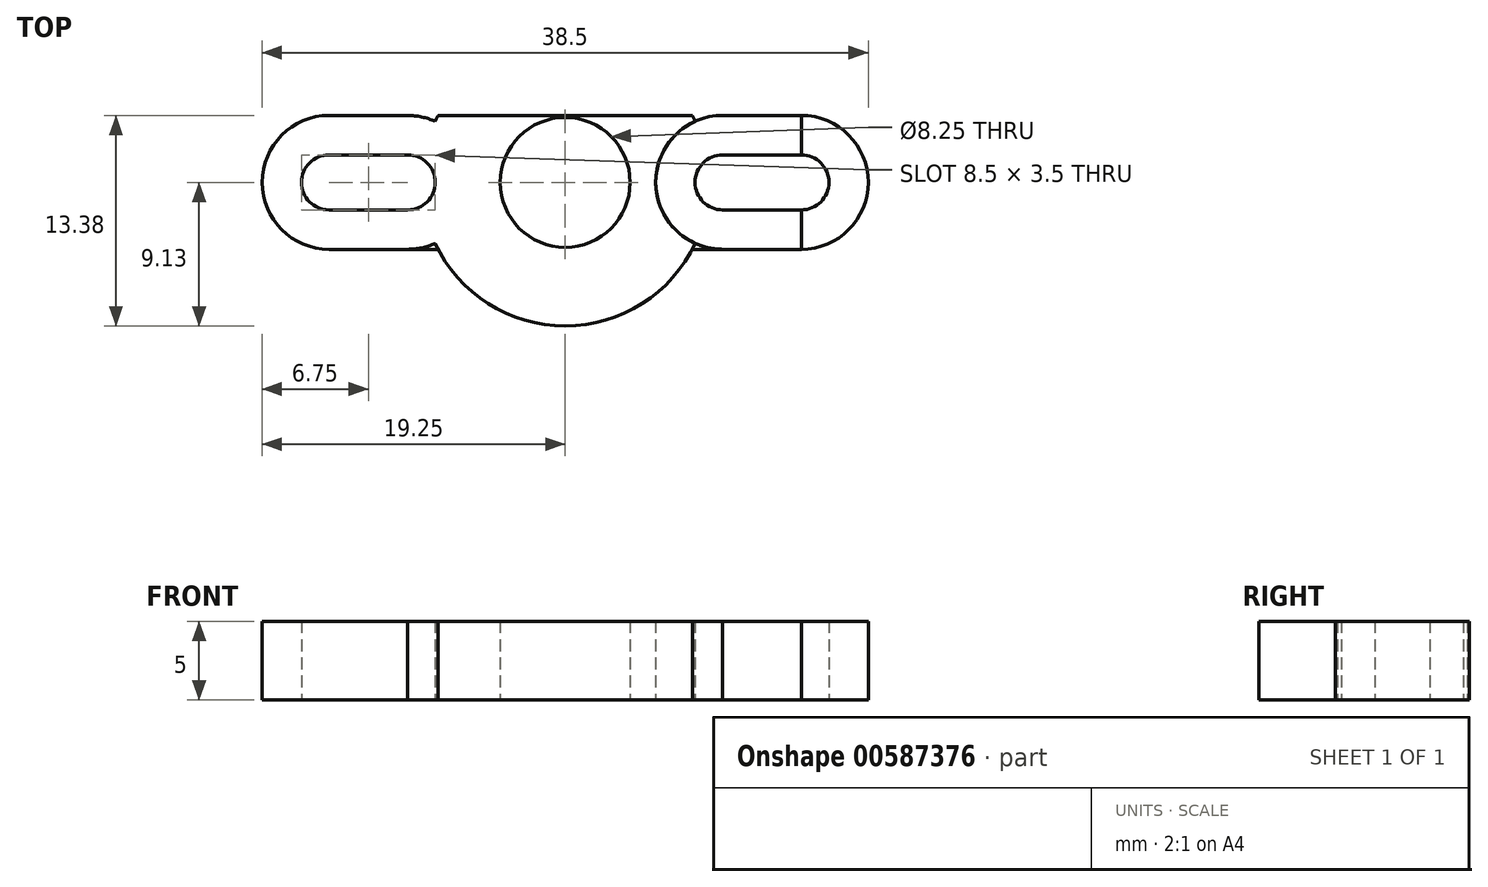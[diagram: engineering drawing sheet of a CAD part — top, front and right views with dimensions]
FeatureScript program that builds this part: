
annotation { "Feature Type Name" : "Feature", "Feature Type Description" : "" }
export const myFeature = defineFeature(function(context is Context, id is Id, definition is map)
    precondition{}
    {
        {
            var Q0;
            Q0=qCreatedBy(makeId("Top.planeOp"),FACE);
            var sketch = newSketch(context, id + "F0", { "sketchPlane" : qUnion([Q0])});
            skCircle(sketch, "E0", {"center": v(0, 0) * mm, "radius": 4.12 * mm});
            skCircle(sketch, "E1", {"center": v(10, 0) * mm, "radius": 1.75 * mm});
            skCircle(sketch, "E2", {"center": v(-10, 0) * mm, "radius": 1.75 * mm});
            skCircle(sketch, "E3", {"center": v(0, 0) * mm, "radius": 9.12 * mm});
            skCircle(sketch, "E4", {"center": v(15, 0) * mm, "radius": 1.75 * mm});
            skCircle(sketch, "E5", {"center": v(-15, 0) * mm, "radius": 1.75 * mm});
            skLineSegment(sketch, "E6.bottom", {"start": v(-15, 1.75) * mm, "end": v(-10, 1.75) * mm});
            skLineSegment(sketch, "E6.top", {"start": v(-15, -1.75) * mm, "end": v(-10, -1.75) * mm});
            skLineSegment(sketch, "E6.left", {"start": v(-15, 1.75) * mm, "end": v(-15, -1.75) * mm});
            skLineSegment(sketch, "E6.right", {"start": v(-10, 1.75) * mm, "end": v(-10, -1.75) * mm});
            skPoint(sketch, "E6.middle", {"position": v(-12.5, 0) * mm});
            skLineSegment(sketch, "E7.bottom", {"start": v(10, 1.75) * mm, "end": v(15, 1.75) * mm});
            skLineSegment(sketch, "E7.top", {"start": v(10, -1.75) * mm, "end": v(15, -1.75) * mm});
            skLineSegment(sketch, "E7.left", {"start": v(10, 1.75) * mm, "end": v(10, -1.75) * mm});
            skLineSegment(sketch, "E7.right", {"start": v(15, 1.75) * mm, "end": v(15, -1.75) * mm});
            skPoint(sketch, "E7.middle", {"position": v(12.5, 0) * mm});
            skCircle(sketch, "E8", {"center": v(-15, 0) * mm, "radius": 4.25 * mm});
            skCircle(sketch, "E9", {"center": v(15, 0) * mm, "radius": 4.25 * mm});
            skCircle(sketch, "E10", {"center": v(-10, 0) * mm, "radius": 4.25 * mm});
            skCircle(sketch, "E11", {"center": v(10, 0) * mm, "radius": 4.25 * mm});
            skLineSegment(sketch, "E12.bottom", {"start": v(-15, 4.25) * mm, "end": v(15, 4.25) * mm});
            skLineSegment(sketch, "E12.top", {"start": v(-15, -4.25) * mm, "end": v(15, -4.25) * mm});
            skLineSegment(sketch, "E12.left", {"start": v(-15, 4.25) * mm, "end": v(-15, -4.25) * mm});
            skLineSegment(sketch, "E12.right", {"start": v(15, 4.25) * mm, "end": v(15, -4.25) * mm});
            skSolve(sketch);
        }
        {
            var Q0;
            {var subQ0=sQuery(id+"F0.wireOp",EDGE,"E12.bottom");var subQ1=sQuery(id+"F0.wireOp",EDGE,"E3");var subQ2=makeQuery(id+"F0.imprint","INTERSECT",VERTEX,{"disambiguationData":[OD(0.0)],"derivedFrom":[subQ1,subQ0]});Q0=makeQuery(id+"F0.imprint","IMPRINT",FACE,{"disambiguationData":[TD([[makeQuery(id+"F0.imprint","IMPRINT",EDGE,{"disambiguationData":[TD([[subQ2,-1.0]])],"derivedFrom":subQ1}),1.0]])]});}
            var Q1;
            Q1=makeQuery(id+"F0.imprint","IMPRINT",FACE,{"disambiguationData":[TD([[makeQuery(id+"F0.imprint","IMPRINT",EDGE,{"derivedFrom":sQuery(id+"F0.wireOp",EDGE,"E0")}),-1.0]])]});
            var Q2;
            {var subQ0=sQuery(id+"F0.wireOp",EDGE,"E12.top");var subQ1=sQuery(id+"F0.wireOp",EDGE,"E3");var subQ2=makeQuery(id+"F0.imprint","INTERSECT",VERTEX,{"disambiguationData":[OD(0.0)],"derivedFrom":[subQ1,subQ0]});Q2=makeQuery(id+"F0.imprint","IMPRINT",FACE,{"disambiguationData":[TD([[makeQuery(id+"F0.imprint","IMPRINT",EDGE,{"disambiguationData":[TD([[subQ2,-1.0]])],"derivedFrom":subQ1}),1.0]])]});}
            var Q3;
            {var subQ0=sQuery(id+"F0.wireOp",EDGE,"E3");var subQ1=sQuery(id+"F0.wireOp",EDGE,"E2");var subQ2=makeQuery(id+"F0.imprint","INTERSECT",VERTEX,{"disambiguationData":[OD(0.0)],"derivedFrom":[subQ1,subQ0]});Q3=makeQuery(id+"F0.imprint","IMPRINT",FACE,{"disambiguationData":[TD([[makeQuery(id+"F0.imprint","IMPRINT",EDGE,{"disambiguationData":[TD([[subQ2,1.0]])],"derivedFrom":subQ1}),-1.0]])]});}
            var Q4;
            {var subQ5=sQuery(id+"F0.wireOp",EDGE,"E2");var subQ7=sQuery(id+"F0.wireOp",EDGE,"E3");var subQ8=makeQuery(id+"F0.imprint","INTERSECT",VERTEX,{"disambiguationData":[OD(0.0)],"derivedFrom":[subQ5,subQ7]});Q4=makeQuery(id+"F0.imprint","IMPRINT",FACE,{"disambiguationData":[TD([[makeQuery(id+"F0.imprint","IMPRINT",EDGE,{"disambiguationData":[TD([[subQ8,1.0]])],"derivedFrom":subQ7}),-1.0]])]});}
            var Q5;
            {var subQ0=sQuery(id+"F0.wireOp",EDGE,"E12.bottom");var subQ3=sQuery(id+"F0.wireOp",EDGE,"E10");var subQ5=makeQuery(id+"F0.imprint","INTERSECT",VERTEX,{"derivedFrom":[subQ3,subQ0]});Q5=makeQuery(id+"F0.imprint","IMPRINT",FACE,{"disambiguationData":[TD([[makeQuery(id+"F0.imprint","IMPRINT",EDGE,{"disambiguationData":[TD([[subQ5,-1.0]])],"derivedFrom":subQ3}),-1.0]])]});}
            var Q6;
            {var subQ1=sQuery(id+"F0.wireOp",EDGE,"E6.bottom");var subQ3=sQuery(id+"F0.wireOp",EDGE,"E10");var subQ4=makeQuery(id+"F0.imprint","INTERSECT",VERTEX,{"derivedFrom":[subQ1,subQ3]});Q6=makeQuery(id+"F0.imprint","IMPRINT",FACE,{"disambiguationData":[TD([[makeQuery(id+"F0.imprint","IMPRINT",EDGE,{"disambiguationData":[TD([[subQ4,1.0]])],"derivedFrom":subQ3}),-1.0]])]});}
            var Q7;
            {var subQ0=sQuery(id+"F0.wireOp",EDGE,"E12.left");var subQ1=sQuery(id+"F0.wireOp",EDGE,"E5");var subQ2=makeQuery(id+"F0.imprint","INTERSECT",VERTEX,{"derivedFrom":[subQ1,sQuery(id+"F0.wireOp",EDGE,"E6.bottom"),subQ0]});Q7=makeQuery(id+"F0.imprint","IMPRINT",FACE,{"disambiguationData":[TD([[makeQuery(id+"F0.imprint","IMPRINT",EDGE,{"disambiguationData":[TD([[subQ2,-1.0]])],"derivedFrom":subQ1}),-1.0]])]});}
            var Q8;
            {var subQ0=sQuery(id+"F0.wireOp",EDGE,"E10");var subQ1=sQuery(id+"F0.wireOp",EDGE,"E6.bottom");var subQ2=makeQuery(id+"F0.imprint","INTERSECT",VERTEX,{"derivedFrom":[subQ1,subQ0]});Q8=makeQuery(id+"F0.imprint","IMPRINT",FACE,{"disambiguationData":[TD([[makeQuery(id+"F0.imprint","IMPRINT",EDGE,{"disambiguationData":[TD([[subQ2,-1.0]])],"derivedFrom":subQ1}),1.0]])]});}
            var Q9;
            {var subQ3=sQuery(id+"F0.wireOp",EDGE,"E8");var subQ11=sQuery(id+"F0.wireOp",EDGE,"E2");var subQ12=makeQuery(id+"F0.imprint","INTERSECT",VERTEX,{"disambiguationData":[OD(0.0)],"derivedFrom":[subQ11,subQ3]});Q9=makeQuery(id+"F0.imprint","IMPRINT",FACE,{"disambiguationData":[TD([[makeQuery(id+"F0.imprint","IMPRINT",EDGE,{"disambiguationData":[TD([[subQ12,-1.0]])],"derivedFrom":subQ11}),-1.0]])]});}
            var Q10;
            {var subQ1=sQuery(id+"F0.wireOp",EDGE,"E6.top");var subQ3=sQuery(id+"F0.wireOp",EDGE,"E10");var subQ4=makeQuery(id+"F0.imprint","INTERSECT",VERTEX,{"derivedFrom":[subQ1,subQ3]});Q10=makeQuery(id+"F0.imprint","IMPRINT",FACE,{"disambiguationData":[TD([[makeQuery(id+"F0.imprint","IMPRINT",EDGE,{"disambiguationData":[TD([[subQ4,-1.0]])],"derivedFrom":subQ3}),-1.0]])]});}
            var Q11;
            {var subQ0=sQuery(id+"F0.wireOp",EDGE,"E10");var subQ1=sQuery(id+"F0.wireOp",EDGE,"E6.top");var subQ2=makeQuery(id+"F0.imprint","INTERSECT",VERTEX,{"derivedFrom":[subQ1,subQ0]});Q11=makeQuery(id+"F0.imprint","IMPRINT",FACE,{"disambiguationData":[TD([[makeQuery(id+"F0.imprint","IMPRINT",EDGE,{"disambiguationData":[TD([[subQ2,-1.0]])],"derivedFrom":subQ1}),-1.0]])]});}
            var Q12;
            {var subQ5=sQuery(id+"F0.wireOp",EDGE,"E3");var subQ6=sQuery(id+"F0.wireOp",EDGE,"E2");var subQ7=makeQuery(id+"F0.imprint","INTERSECT",VERTEX,{"disambiguationData":[OD(1.0)],"derivedFrom":[subQ6,subQ5]});Q12=makeQuery(id+"F0.imprint","IMPRINT",FACE,{"disambiguationData":[TD([[makeQuery(id+"F0.imprint","IMPRINT",EDGE,{"disambiguationData":[TD([[subQ7,-1.0]])],"derivedFrom":subQ5}),-1.0]])]});}
            var Q13;
            {var subQ0=sQuery(id+"F0.wireOp",EDGE,"E12.top");var subQ3=sQuery(id+"F0.wireOp",EDGE,"E10");var subQ5=makeQuery(id+"F0.imprint","INTERSECT",VERTEX,{"derivedFrom":[subQ3,subQ0]});Q13=makeQuery(id+"F0.imprint","IMPRINT",FACE,{"disambiguationData":[TD([[makeQuery(id+"F0.imprint","IMPRINT",EDGE,{"disambiguationData":[TD([[subQ5,1.0]])],"derivedFrom":subQ3}),-1.0]])]});}
            var Q14;
            {var subQ1=sQuery(id+"F0.wireOp",EDGE,"E5");var subQ3=sQuery(id+"F0.wireOp",EDGE,"E10");var subQ4=makeQuery(id+"F0.imprint","INTERSECT",VERTEX,{"disambiguationData":[OD(0.0)],"derivedFrom":[subQ1,subQ3]});Q14=makeQuery(id+"F0.imprint","IMPRINT",FACE,{"disambiguationData":[TD([[makeQuery(id+"F0.imprint","IMPRINT",EDGE,{"disambiguationData":[TD([[subQ4,1.0]])],"derivedFrom":subQ3}),-1.0]])]});}
            var Q15;
            {var subQ1=sQuery(id+"F0.wireOp",EDGE,"E2");var subQ3=sQuery(id+"F0.wireOp",EDGE,"E8");var subQ4=makeQuery(id+"F0.imprint","INTERSECT",VERTEX,{"disambiguationData":[OD(0.0)],"derivedFrom":[subQ1,subQ3]});Q15=makeQuery(id+"F0.imprint","IMPRINT",FACE,{"disambiguationData":[TD([[makeQuery(id+"F0.imprint","IMPRINT",EDGE,{"disambiguationData":[TD([[subQ4,-1.0]])],"derivedFrom":subQ3}),-1.0]])]});}
            var Q16;
            {var subQ1=sQuery(id+"F0.wireOp",EDGE,"E5");var subQ3=sQuery(id+"F0.wireOp",EDGE,"E10");var subQ4=makeQuery(id+"F0.imprint","INTERSECT",VERTEX,{"disambiguationData":[OD(1.0)],"derivedFrom":[subQ1,subQ3]});Q16=makeQuery(id+"F0.imprint","IMPRINT",FACE,{"disambiguationData":[TD([[makeQuery(id+"F0.imprint","IMPRINT",EDGE,{"disambiguationData":[TD([[subQ4,-1.0]])],"derivedFrom":subQ3}),-1.0]])]});}
            var Q17;
            {var subQ1=sQuery(id+"F0.wireOp",EDGE,"E2");var subQ3=sQuery(id+"F0.wireOp",EDGE,"E8");var subQ4=makeQuery(id+"F0.imprint","INTERSECT",VERTEX,{"disambiguationData":[OD(1.0)],"derivedFrom":[subQ1,subQ3]});Q17=makeQuery(id+"F0.imprint","IMPRINT",FACE,{"disambiguationData":[TD([[makeQuery(id+"F0.imprint","IMPRINT",EDGE,{"disambiguationData":[TD([[subQ4,1.0]])],"derivedFrom":subQ3}),-1.0]])]});}
            var Q18;
            {var subQ0=sQuery(id+"F0.wireOp",EDGE,"E12.right");var subQ1=sQuery(id+"F0.wireOp",EDGE,"E4");var subQ2=makeQuery(id+"F0.imprint","INTERSECT",VERTEX,{"derivedFrom":[subQ1,sQuery(id+"F0.wireOp",EDGE,"E7.bottom"),subQ0]});Q18=makeQuery(id+"F0.imprint","IMPRINT",FACE,{"disambiguationData":[TD([[makeQuery(id+"F0.imprint","IMPRINT",EDGE,{"disambiguationData":[TD([[subQ2,1.0]])],"derivedFrom":subQ1}),-1.0]])]});}
            var Q19;
            {var subQ0=sQuery(id+"F0.wireOp",EDGE,"E9");var subQ1=sQuery(id+"F0.wireOp",EDGE,"E7.bottom");var subQ2=makeQuery(id+"F0.imprint","INTERSECT",VERTEX,{"derivedFrom":[subQ1,subQ0]});Q19=makeQuery(id+"F0.imprint","IMPRINT",FACE,{"disambiguationData":[TD([[makeQuery(id+"F0.imprint","IMPRINT",EDGE,{"disambiguationData":[TD([[subQ2,-1.0]])],"derivedFrom":subQ1}),1.0]])]});}
            var Q20;
            {var subQ0=sQuery(id+"F0.wireOp",EDGE,"E9");var subQ11=sQuery(id+"F0.wireOp",EDGE,"E1");var subQ13=makeQuery(id+"F0.imprint","INTERSECT",VERTEX,{"disambiguationData":[OD(0.0)],"derivedFrom":[subQ11,subQ0]});Q20=makeQuery(id+"F0.imprint","IMPRINT",FACE,{"disambiguationData":[TD([[makeQuery(id+"F0.imprint","IMPRINT",EDGE,{"disambiguationData":[TD([[subQ13,1.0]])],"derivedFrom":subQ11}),-1.0]])]});}
            var Q21;
            {var subQ1=sQuery(id+"F0.wireOp",EDGE,"E4");var subQ3=sQuery(id+"F0.wireOp",EDGE,"E11");var subQ4=makeQuery(id+"F0.imprint","INTERSECT",VERTEX,{"disambiguationData":[OD(1.0)],"derivedFrom":[subQ1,subQ3]});Q21=makeQuery(id+"F0.imprint","IMPRINT",FACE,{"disambiguationData":[TD([[makeQuery(id+"F0.imprint","IMPRINT",EDGE,{"disambiguationData":[TD([[subQ4,1.0]])],"derivedFrom":subQ3}),-1.0]])]});}
            var Q22;
            {var subQ1=sQuery(id+"F0.wireOp",EDGE,"E4");var subQ3=sQuery(id+"F0.wireOp",EDGE,"E11");var subQ4=makeQuery(id+"F0.imprint","INTERSECT",VERTEX,{"disambiguationData":[OD(0.0)],"derivedFrom":[subQ1,subQ3]});Q22=makeQuery(id+"F0.imprint","IMPRINT",FACE,{"disambiguationData":[TD([[makeQuery(id+"F0.imprint","IMPRINT",EDGE,{"disambiguationData":[TD([[subQ4,-1.0]])],"derivedFrom":subQ3}),-1.0]])]});}
            extrude(context, id + "F1", {"entities" : qUnion([Q0, Q1, Q2, Q3, Q4, Q5, Q6, Q7, Q8, Q9, Q10, Q11, Q12, Q13, Q14, Q15, Q16, Q17, Q18, Q19, Q20, Q21, Q22]), "depth" : 5 * mm, "offsetDistance" : 25 * mm});
        }
        {
            var Q0;
            {var subQ1=sQuery(id+"F0.wireOp",EDGE,"E7.bottom");var subQ3=sQuery(id+"F0.wireOp",EDGE,"E11");var subQ4=makeQuery(id+"F0.imprint","INTERSECT",VERTEX,{"derivedFrom":[subQ1,subQ3]});Q0=makeQuery(id+"F0.imprint","IMPRINT",FACE,{"disambiguationData":[TD([[makeQuery(id+"F0.imprint","IMPRINT",EDGE,{"disambiguationData":[TD([[subQ4,-1.0]])],"derivedFrom":subQ3}),-1.0]])]});}
            var Q1;
            {var subQ0=sQuery(id+"F0.wireOp",EDGE,"E12.bottom");var subQ3=sQuery(id+"F0.wireOp",EDGE,"E11");var subQ5=makeQuery(id+"F0.imprint","INTERSECT",VERTEX,{"derivedFrom":[subQ3,subQ0]});Q1=makeQuery(id+"F0.imprint","IMPRINT",FACE,{"disambiguationData":[TD([[makeQuery(id+"F0.imprint","IMPRINT",EDGE,{"disambiguationData":[TD([[subQ5,1.0]])],"derivedFrom":subQ3}),-1.0]])]});}
            var Q2;
            {var subQ5=sQuery(id+"F0.wireOp",EDGE,"E1");var subQ7=sQuery(id+"F0.wireOp",EDGE,"E3");var subQ8=makeQuery(id+"F0.imprint","INTERSECT",VERTEX,{"disambiguationData":[OD(0.0)],"derivedFrom":[subQ5,subQ7]});Q2=makeQuery(id+"F0.imprint","IMPRINT",FACE,{"disambiguationData":[TD([[makeQuery(id+"F0.imprint","IMPRINT",EDGE,{"disambiguationData":[TD([[subQ8,-1.0]])],"derivedFrom":subQ7}),-1.0]])]});}
            var Q3;
            {var subQ0=sQuery(id+"F0.wireOp",EDGE,"E3");var subQ1=sQuery(id+"F0.wireOp",EDGE,"E1");var subQ2=makeQuery(id+"F0.imprint","INTERSECT",VERTEX,{"disambiguationData":[OD(0.0)],"derivedFrom":[subQ1,subQ0]});Q3=makeQuery(id+"F0.imprint","IMPRINT",FACE,{"disambiguationData":[TD([[makeQuery(id+"F0.imprint","IMPRINT",EDGE,{"disambiguationData":[TD([[subQ2,-1.0]])],"derivedFrom":subQ1}),-1.0]])]});}
            var Q4;
            {var subQ1=sQuery(id+"F0.wireOp",EDGE,"E7.top");var subQ3=sQuery(id+"F0.wireOp",EDGE,"E11");var subQ4=makeQuery(id+"F0.imprint","INTERSECT",VERTEX,{"derivedFrom":[subQ1,subQ3]});Q4=makeQuery(id+"F0.imprint","IMPRINT",FACE,{"disambiguationData":[TD([[makeQuery(id+"F0.imprint","IMPRINT",EDGE,{"disambiguationData":[TD([[subQ4,1.0]])],"derivedFrom":subQ3}),-1.0]])]});}
            var Q5;
            {var subQ0=sQuery(id+"F0.wireOp",EDGE,"E12.top");var subQ3=sQuery(id+"F0.wireOp",EDGE,"E11");var subQ5=makeQuery(id+"F0.imprint","INTERSECT",VERTEX,{"derivedFrom":[subQ3,subQ0]});Q5=makeQuery(id+"F0.imprint","IMPRINT",FACE,{"disambiguationData":[TD([[makeQuery(id+"F0.imprint","IMPRINT",EDGE,{"disambiguationData":[TD([[subQ5,-1.0]])],"derivedFrom":subQ3}),-1.0]])]});}
            var Q6;
            {var subQ5=sQuery(id+"F0.wireOp",EDGE,"E1");var subQ7=sQuery(id+"F0.wireOp",EDGE,"E3");var subQ8=makeQuery(id+"F0.imprint","INTERSECT",VERTEX,{"disambiguationData":[OD(1.0)],"derivedFrom":[subQ5,subQ7]});Q6=makeQuery(id+"F0.imprint","IMPRINT",FACE,{"disambiguationData":[TD([[makeQuery(id+"F0.imprint","IMPRINT",EDGE,{"disambiguationData":[TD([[subQ8,1.0]])],"derivedFrom":subQ7}),-1.0]])]});}
            var Q7;
            {var subQ0=sQuery(id+"F0.wireOp",EDGE,"E9");var subQ1=sQuery(id+"F0.wireOp",EDGE,"E7.top");var subQ2=makeQuery(id+"F0.imprint","INTERSECT",VERTEX,{"derivedFrom":[subQ1,subQ0]});Q7=makeQuery(id+"F0.imprint","IMPRINT",FACE,{"disambiguationData":[TD([[makeQuery(id+"F0.imprint","IMPRINT",EDGE,{"disambiguationData":[TD([[subQ2,-1.0]])],"derivedFrom":subQ1}),-1.0]])]});}
            var Q8;
            {var subQ1=sQuery(id+"F0.wireOp",EDGE,"E1");var subQ3=sQuery(id+"F0.wireOp",EDGE,"E9");var subQ4=makeQuery(id+"F0.imprint","INTERSECT",VERTEX,{"disambiguationData":[OD(0.0)],"derivedFrom":[subQ1,subQ3]});Q8=makeQuery(id+"F0.imprint","IMPRINT",FACE,{"disambiguationData":[TD([[makeQuery(id+"F0.imprint","IMPRINT",EDGE,{"disambiguationData":[TD([[subQ4,1.0]])],"derivedFrom":subQ3}),-1.0]])]});}
            var Q9;
            {var subQ1=sQuery(id+"F0.wireOp",EDGE,"E1");var subQ3=sQuery(id+"F0.wireOp",EDGE,"E9");var subQ4=makeQuery(id+"F0.imprint","INTERSECT",VERTEX,{"disambiguationData":[OD(1.0)],"derivedFrom":[subQ1,subQ3]});Q9=makeQuery(id+"F0.imprint","IMPRINT",FACE,{"disambiguationData":[TD([[makeQuery(id+"F0.imprint","IMPRINT",EDGE,{"disambiguationData":[TD([[subQ4,-1.0]])],"derivedFrom":subQ3}),-1.0]])]});}
            extrude(context, id + "F2", {"entities" : qUnion([Q0, Q1, Q2, Q3, Q4, Q5, Q6, Q7, Q8, Q9]), "depth" : 5 * mm, "offsetDistance" : 25 * mm});
        }
        {
            var Q0;
            {var subQ0=sQuery(id+"F0.wireOp",EDGE,"E12.bottom");var subQ1=sQuery(id+"F0.wireOp",EDGE,"E3");var subQ2=makeQuery(id+"F0.imprint","INTERSECT",VERTEX,{"disambiguationData":[OD(0.0)],"derivedFrom":[subQ1,subQ0]});Q0=makeQuery(id+"F0.imprint","IMPRINT",FACE,{"disambiguationData":[TD([[makeQuery(id+"F0.imprint","IMPRINT",EDGE,{"disambiguationData":[TD([[subQ2,1.0]])],"derivedFrom":subQ1}),-1.0]])]});}
            var Q1;
            {var subQ0=sQuery(id+"F0.wireOp",EDGE,"E12.top");var subQ1=sQuery(id+"F0.wireOp",EDGE,"E3");var subQ2=makeQuery(id+"F0.imprint","INTERSECT",VERTEX,{"disambiguationData":[OD(1.0)],"derivedFrom":[subQ1,subQ0]});Q1=makeQuery(id+"F0.imprint","IMPRINT",FACE,{"disambiguationData":[TD([[makeQuery(id+"F0.imprint","IMPRINT",EDGE,{"disambiguationData":[TD([[subQ2,-1.0]])],"derivedFrom":subQ1}),-1.0]])]});}
            var Q2;
            {var subQ0=sQuery(id+"F0.wireOp",EDGE,"E12.top");var subQ1=sQuery(id+"F0.wireOp",EDGE,"E3");var subQ2=makeQuery(id+"F0.imprint","INTERSECT",VERTEX,{"disambiguationData":[OD(0.0)],"derivedFrom":[subQ1,subQ0]});Q2=makeQuery(id+"F0.imprint","IMPRINT",FACE,{"disambiguationData":[TD([[makeQuery(id+"F0.imprint","IMPRINT",EDGE,{"disambiguationData":[TD([[subQ2,1.0]])],"derivedFrom":subQ1}),-1.0]])]});}
            var Q3;
            {var subQ0=sQuery(id+"F0.wireOp",EDGE,"E12.bottom");var subQ1=sQuery(id+"F0.wireOp",EDGE,"E3");var subQ2=makeQuery(id+"F0.imprint","INTERSECT",VERTEX,{"disambiguationData":[OD(1.0)],"derivedFrom":[subQ1,subQ0]});Q3=makeQuery(id+"F0.imprint","IMPRINT",FACE,{"disambiguationData":[TD([[makeQuery(id+"F0.imprint","IMPRINT",EDGE,{"disambiguationData":[TD([[subQ2,-1.0]])],"derivedFrom":subQ1}),-1.0]])]});}
            extrude(context, id + "F3", {"entities" : qUnion([Q0, Q1, Q2, Q3]), "depth" : 5 * mm, "offsetDistance" : 25 * mm});
        }
        {
            var Q0;
            {var subQ0=sQuery(id+"F0.wireOp",EDGE,"E9");var subQ1=sQuery(id+"F0.wireOp",EDGE,"E1");var subQ2=makeQuery(id+"F0.imprint","INTERSECT",VERTEX,{"disambiguationData":[OD(0.0)],"derivedFrom":[subQ1,subQ0]});Q0=makeQuery(id+"F0.imprint","IMPRINT",FACE,{"disambiguationData":[TD([[makeQuery(id+"F0.imprint","IMPRINT",EDGE,{"disambiguationData":[TD([[subQ2,1.0]])],"derivedFrom":subQ1}),1.0]])]});}
            var Q1;
            {var subQ0=sQuery(id+"F0.wireOp",EDGE,"E7.left");Q1=makeQuery(id+"F0.imprint","IMPRINT",FACE,{"disambiguationData":[TD([[makeQuery(id+"F0.imprint","IMPRINT",EDGE,{"derivedFrom":subQ0}),-1.0]])]});}
            var Q2;
            {var subQ0=sQuery(id+"F0.wireOp",EDGE,"E3");var subQ1=sQuery(id+"F0.wireOp",EDGE,"E1");var subQ2=makeQuery(id+"F0.imprint","INTERSECT",VERTEX,{"disambiguationData":[OD(0.0)],"derivedFrom":[subQ1,subQ0]});Q2=makeQuery(id+"F0.imprint","IMPRINT",FACE,{"disambiguationData":[TD([[makeQuery(id+"F0.imprint","IMPRINT",EDGE,{"disambiguationData":[TD([[subQ2,-1.0]])],"derivedFrom":subQ1}),1.0]])]});}
            var Q3;
            {var subQ0=sQuery(id+"F0.wireOp",EDGE,"E7.left");Q3=makeQuery(id+"F0.imprint","IMPRINT",FACE,{"disambiguationData":[TD([[makeQuery(id+"F0.imprint","IMPRINT",EDGE,{"derivedFrom":subQ0}),1.0]])]});}
            extrude(context, id + "F4", {"entities" : qUnion([Q0, Q1, Q2, Q3]), "operationType" : NewBodyOperationType.ADD, "depth" : 5 * mm, "offsetDistance" : 25 * mm});
        }
        {
            var Q0;
            {var subQ3=sQuery(id+"F0.wireOp",EDGE,"E8");var subQ11=sQuery(id+"F0.wireOp",EDGE,"E2");var subQ12=makeQuery(id+"F0.imprint","INTERSECT",VERTEX,{"disambiguationData":[OD(0.0)],"derivedFrom":[subQ11,subQ3]});Q0=makeQuery(id+"F0.imprint","IMPRINT",FACE,{"disambiguationData":[TD([[makeQuery(id+"F0.imprint","IMPRINT",EDGE,{"disambiguationData":[TD([[subQ12,-1.0]])],"derivedFrom":subQ11}),-1.0]])]});}
            var Q1;
            {var subQ1=sQuery(id+"F0.wireOp",EDGE,"E5");var subQ3=sQuery(id+"F0.wireOp",EDGE,"E10");var subQ4=makeQuery(id+"F0.imprint","INTERSECT",VERTEX,{"disambiguationData":[OD(1.0)],"derivedFrom":[subQ1,subQ3]});Q1=makeQuery(id+"F0.imprint","IMPRINT",FACE,{"disambiguationData":[TD([[makeQuery(id+"F0.imprint","IMPRINT",EDGE,{"disambiguationData":[TD([[subQ4,-1.0]])],"derivedFrom":subQ3}),-1.0]])]});}
            var Q2;
            {var subQ1=sQuery(id+"F0.wireOp",EDGE,"E5");var subQ3=sQuery(id+"F0.wireOp",EDGE,"E10");var subQ4=makeQuery(id+"F0.imprint","INTERSECT",VERTEX,{"disambiguationData":[OD(0.0)],"derivedFrom":[subQ1,subQ3]});Q2=makeQuery(id+"F0.imprint","IMPRINT",FACE,{"disambiguationData":[TD([[makeQuery(id+"F0.imprint","IMPRINT",EDGE,{"disambiguationData":[TD([[subQ4,1.0]])],"derivedFrom":subQ3}),-1.0]])]});}
            var Q3;
            {var subQ1=sQuery(id+"F0.wireOp",EDGE,"E2");var subQ3=sQuery(id+"F0.wireOp",EDGE,"E8");var subQ4=makeQuery(id+"F0.imprint","INTERSECT",VERTEX,{"disambiguationData":[OD(0.0)],"derivedFrom":[subQ1,subQ3]});Q3=makeQuery(id+"F0.imprint","IMPRINT",FACE,{"disambiguationData":[TD([[makeQuery(id+"F0.imprint","IMPRINT",EDGE,{"disambiguationData":[TD([[subQ4,-1.0]])],"derivedFrom":subQ3}),-1.0]])]});}
            var Q4;
            {var subQ1=sQuery(id+"F0.wireOp",EDGE,"E2");var subQ3=sQuery(id+"F0.wireOp",EDGE,"E8");var subQ4=makeQuery(id+"F0.imprint","INTERSECT",VERTEX,{"disambiguationData":[OD(1.0)],"derivedFrom":[subQ1,subQ3]});Q4=makeQuery(id+"F0.imprint","IMPRINT",FACE,{"disambiguationData":[TD([[makeQuery(id+"F0.imprint","IMPRINT",EDGE,{"disambiguationData":[TD([[subQ4,1.0]])],"derivedFrom":subQ3}),-1.0]])]});}
            extrude(context, id + "F5", {"entities" : qUnion([Q0, Q1, Q2, Q3, Q4]), "operationType" : NewBodyOperationType.REMOVE, "depth" : 25 * mm, "offsetDistance" : 25 * mm});
        }
        {
            var Q0;
            {var subQ0=sQuery(id+"F0.wireOp",EDGE,"E3");var subQ1=sQuery(id+"F0.wireOp",EDGE,"E1");var subQ2=makeQuery(id+"F0.imprint","INTERSECT",VERTEX,{"disambiguationData":[OD(0.0)],"derivedFrom":[subQ1,subQ0]});Q0=makeQuery(id+"F0.imprint","IMPRINT",FACE,{"disambiguationData":[TD([[makeQuery(id+"F0.imprint","IMPRINT",EDGE,{"disambiguationData":[TD([[subQ2,-1.0]])],"derivedFrom":subQ1}),1.0]])]});}
            var Q1;
            {var subQ0=sQuery(id+"F0.wireOp",EDGE,"E7.left");Q1=makeQuery(id+"F0.imprint","IMPRINT",FACE,{"disambiguationData":[TD([[makeQuery(id+"F0.imprint","IMPRINT",EDGE,{"derivedFrom":subQ0}),-1.0]])]});}
            var Q2;
            {var subQ0=sQuery(id+"F0.wireOp",EDGE,"E7.left");Q2=makeQuery(id+"F0.imprint","IMPRINT",FACE,{"disambiguationData":[TD([[makeQuery(id+"F0.imprint","IMPRINT",EDGE,{"derivedFrom":subQ0}),1.0]])]});}
            var Q3;
            {var subQ0=sQuery(id+"F0.wireOp",EDGE,"E9");var subQ1=sQuery(id+"F0.wireOp",EDGE,"E1");var subQ2=makeQuery(id+"F0.imprint","INTERSECT",VERTEX,{"disambiguationData":[OD(0.0)],"derivedFrom":[subQ1,subQ0]});Q3=makeQuery(id+"F0.imprint","IMPRINT",FACE,{"disambiguationData":[TD([[makeQuery(id+"F0.imprint","IMPRINT",EDGE,{"disambiguationData":[TD([[subQ2,1.0]])],"derivedFrom":subQ1}),1.0]])]});}
            var Q4;
            {var subQ1=sQuery(id+"F0.wireOp",EDGE,"E1");var subQ3=sQuery(id+"F0.wireOp",EDGE,"E9");var subQ4=makeQuery(id+"F0.imprint","INTERSECT",VERTEX,{"disambiguationData":[OD(1.0)],"derivedFrom":[subQ1,subQ3]});Q4=makeQuery(id+"F0.imprint","IMPRINT",FACE,{"disambiguationData":[TD([[makeQuery(id+"F0.imprint","IMPRINT",EDGE,{"disambiguationData":[TD([[subQ4,-1.0]])],"derivedFrom":subQ3}),-1.0]])]});}
            var Q5;
            {var subQ1=sQuery(id+"F0.wireOp",EDGE,"E1");var subQ3=sQuery(id+"F0.wireOp",EDGE,"E9");var subQ4=makeQuery(id+"F0.imprint","INTERSECT",VERTEX,{"disambiguationData":[OD(0.0)],"derivedFrom":[subQ1,subQ3]});Q5=makeQuery(id+"F0.imprint","IMPRINT",FACE,{"disambiguationData":[TD([[makeQuery(id+"F0.imprint","IMPRINT",EDGE,{"disambiguationData":[TD([[subQ4,1.0]])],"derivedFrom":subQ3}),-1.0]])]});}
            var Q6;
            {var subQ1=sQuery(id+"F0.wireOp",EDGE,"E4");var subQ3=sQuery(id+"F0.wireOp",EDGE,"E11");var subQ4=makeQuery(id+"F0.imprint","INTERSECT",VERTEX,{"disambiguationData":[OD(1.0)],"derivedFrom":[subQ1,subQ3]});Q6=makeQuery(id+"F0.imprint","IMPRINT",FACE,{"disambiguationData":[TD([[makeQuery(id+"F0.imprint","IMPRINT",EDGE,{"disambiguationData":[TD([[subQ4,1.0]])],"derivedFrom":subQ3}),-1.0]])]});}
            var Q7;
            {var subQ1=sQuery(id+"F0.wireOp",EDGE,"E4");var subQ3=sQuery(id+"F0.wireOp",EDGE,"E11");var subQ4=makeQuery(id+"F0.imprint","INTERSECT",VERTEX,{"disambiguationData":[OD(0.0)],"derivedFrom":[subQ1,subQ3]});Q7=makeQuery(id+"F0.imprint","IMPRINT",FACE,{"disambiguationData":[TD([[makeQuery(id+"F0.imprint","IMPRINT",EDGE,{"disambiguationData":[TD([[subQ4,-1.0]])],"derivedFrom":subQ3}),-1.0]])]});}
            var Q8;
            {var subQ0=sQuery(id+"F0.wireOp",EDGE,"E9");var subQ11=sQuery(id+"F0.wireOp",EDGE,"E1");var subQ13=makeQuery(id+"F0.imprint","INTERSECT",VERTEX,{"disambiguationData":[OD(0.0)],"derivedFrom":[subQ11,subQ0]});Q8=makeQuery(id+"F0.imprint","IMPRINT",FACE,{"disambiguationData":[TD([[makeQuery(id+"F0.imprint","IMPRINT",EDGE,{"disambiguationData":[TD([[subQ13,1.0]])],"derivedFrom":subQ11}),-1.0]])]});}
            extrude(context, id + "F6", {"entities" : qUnion([Q0, Q1, Q2, Q3, Q4, Q5, Q6, Q7, Q8]), "operationType" : NewBodyOperationType.REMOVE, "depth" : 25 * mm, "offsetDistance" : 25 * mm});
        }
    });
